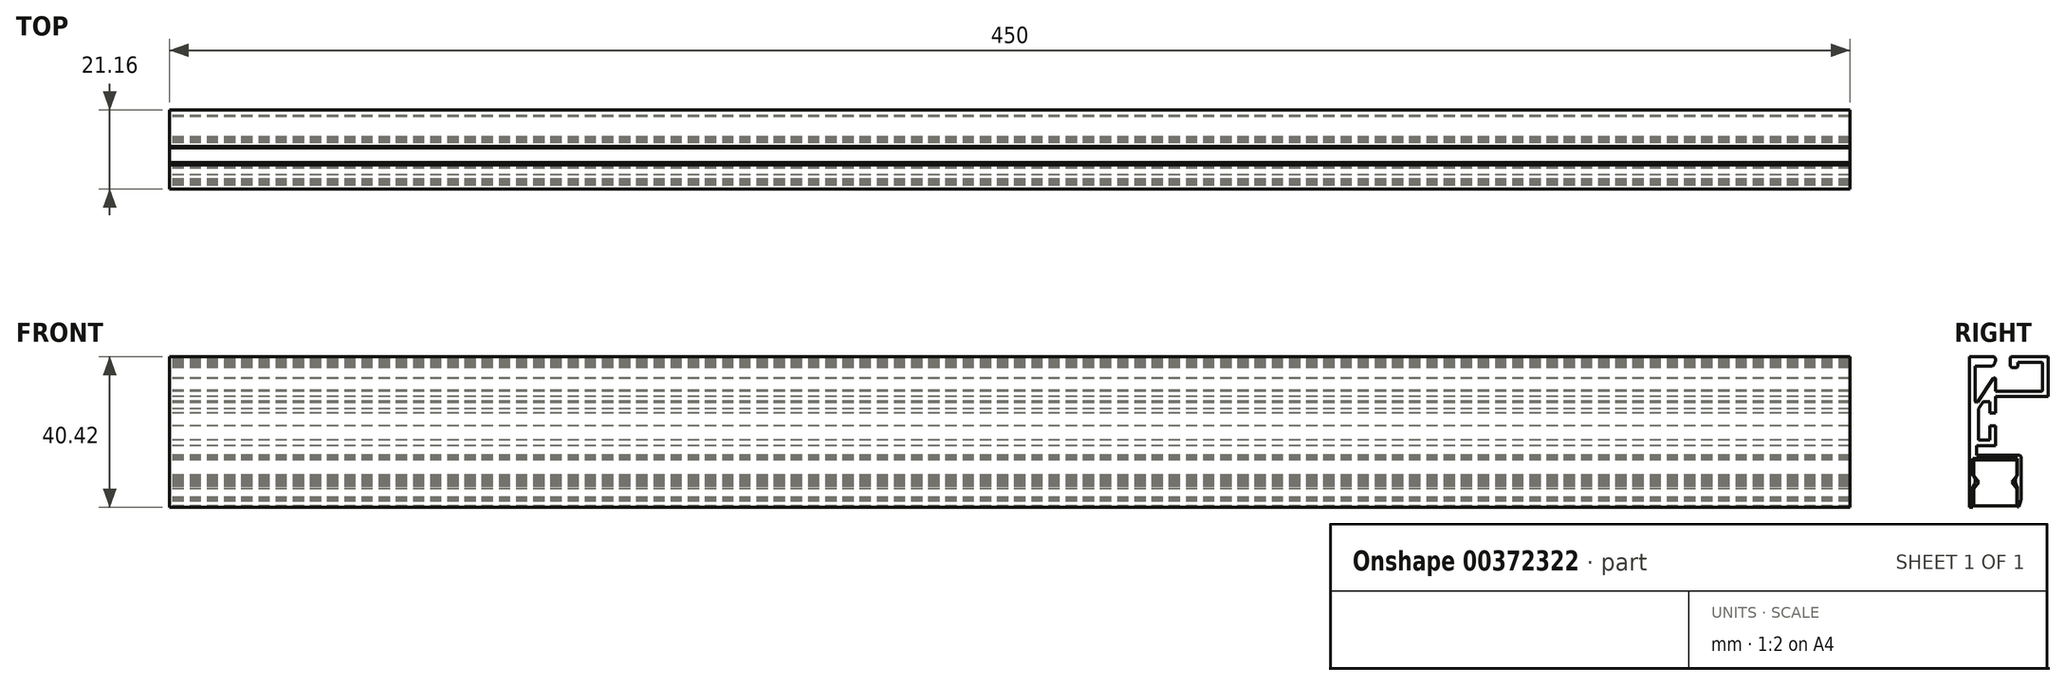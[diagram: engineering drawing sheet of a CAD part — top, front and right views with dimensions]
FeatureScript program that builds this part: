
annotation { "Feature Type Name" : "Feature", "Feature Type Description" : "" }
export const myFeature = defineFeature(function(context is Context, id is Id, definition is map)
    precondition{}
    {
        {
            var Q0;
            Q0=qCreatedBy(makeId("Right.planeOp"),FACE);
            var sketch = newSketch(context, id + "F0", { "sketchPlane" : qUnion([Q0])});
            skLineSegment(sketch, "E0.13", {"start": v(97.95, 20.2) * mm, "end": v(97.95, 9.58) * mm});
            skLineSegment(sketch, "E1.MirrorCS", {"start": v(83.74, 19.84) * mm, "end": v(83.78, 19.62) * mm});
            skLineSegment(sketch, "E2.MirrorCS", {"start": v(83.74, 18.76) * mm, "end": v(83.61, 18.51) * mm});
            skLineSegment(sketch, "E3.MirrorCS", {"start": v(83.78, 19.05) * mm, "end": v(83.74, 18.76) * mm});
            skLineSegment(sketch, "E4.MirrorCS", {"start": v(83.61, 18.51) * mm, "end": v(83.64, 18.5) * mm});
            skLineSegment(sketch, "E5.MirrorCS", {"start": v(83.2, 17.83) * mm, "end": v(83.2, 17.85) * mm});
            skLineSegment(sketch, "E6.MirrorCS", {"start": v(83.64, 18.5) * mm, "end": v(83.2, 17.83) * mm});
            skLineSegment(sketch, "E7.MirrorCS", {"start": v(83.8, 19.62) * mm, "end": v(83.8, 19.05) * mm});
            skLineSegment(sketch, "E8.MirrorCS", {"start": v(83.8, 19.05) * mm, "end": v(83.78, 19.05) * mm});
            skLineSegment(sketch, "E9.MirrorCS", {"start": v(77.92, -14.41) * mm, "end": v(77.8, -14.59) * mm});
            skLineSegment(sketch, "E10.MirrorCS", {"start": v(83.42, 20.16) * mm, "end": v(83.61, 20.04) * mm});
            skLineSegment(sketch, "E11.MirrorCS", {"start": v(82.78, 17.6) * mm, "end": v(82.78, 17.63) * mm});
            skLineSegment(sketch, "E12.MirrorCS", {"start": v(83.8, 19.62) * mm, "end": v(83.78, 19.62) * mm});
            skLineSegment(sketch, "E13.MirrorCS", {"start": v(78.16, -12.18) * mm, "end": v(78.3, -12.6) * mm});
            skLineSegment(sketch, "E14.MirrorCS", {"start": v(78.16, -14.02) * mm, "end": v(77.9, -14.41) * mm});
            skLineSegment(sketch, "E15.MirrorCS", {"start": v(83.2, 20.2) * mm, "end": v(83.42, 20.16) * mm});
            skLineSegment(sketch, "E16.MirrorCS", {"start": v(77.8, -11.61) * mm, "end": v(77.92, -11.79) * mm});
            skLineSegment(sketch, "E17.MirrorCS", {"start": v(83, 17.68) * mm, "end": v(82.78, 17.63) * mm});
            skLineSegment(sketch, "E18.MirrorCS", {"start": v(90.66, -18) * mm, "end": v(90.54, -18.5) * mm});
            skLineSegment(sketch, "E19.MirrorCS", {"start": v(78.3, -12.6) * mm, "end": v(78.36, -13.06) * mm});
            skLineSegment(sketch, "E20.MirrorCS", {"start": v(77.9, -11.79) * mm, "end": v(78.16, -12.18) * mm});
            skLineSegment(sketch, "E21.MirrorCS", {"start": v(83.2, 17.85) * mm, "end": v(83, 17.68) * mm});
            skLineSegment(sketch, "E22.MirrorCS", {"start": v(78.3, -13.6) * mm, "end": v(78.16, -14.02) * mm});
            skLineSegment(sketch, "E23.MirrorCS", {"start": v(83.61, 20.04) * mm, "end": v(83.74, 19.84) * mm});
            skLineSegment(sketch, "E24.MirrorCS", {"start": v(89.73, -14.59) * mm, "end": v(89.58, -14.41) * mm});
            skLineSegment(sketch, "E25.MirrorCS", {"start": v(90.56, -18.5) * mm, "end": v(90.54, -18.5) * mm});
            skLineSegment(sketch, "E26.MirrorCS", {"start": v(77.94, -11.74) * mm, "end": v(79.39, -13.5) * mm});
            skLineSegment(sketch, "E27.MirrorCS", {"start": v(78.36, -13.06) * mm, "end": v(78.36, -13.14) * mm});
            skLineSegment(sketch, "E28.MirrorCS", {"start": v(78.36, -13.14) * mm, "end": v(78.3, -13.6) * mm});
            skLineSegment(sketch, "E29.MirrorCS", {"start": v(77.9, -11.79) * mm, "end": v(77.92, -11.79) * mm});
            skLineSegment(sketch, "E30.MirrorCS", {"start": v(90.56, -18.5) * mm, "end": v(90.02, -20.01) * mm});
            skLineSegment(sketch, "E31.MirrorCS", {"start": v(89.58, -14.41) * mm, "end": v(89.6, -14.41) * mm});
            skLineSegment(sketch, "E32.MirrorCS", {"start": v(77.9, -14.41) * mm, "end": v(77.92, -14.41) * mm});
            skLineSegment(sketch, "E33.MirrorCS", {"start": v(89.33, -14.02) * mm, "end": v(89.19, -13.6) * mm});
            skLineSegment(sketch, "E34.MirrorCS", {"start": v(79.39, -13.5) * mm, "end": v(77.94, -15.25) * mm});
            skLineSegment(sketch, "E35.MirrorCS", {"start": v(89.58, -19.82) * mm, "end": v(89.58, -15.25) * mm});
            skLineSegment(sketch, "E36.MirrorCS", {"start": v(89.73, -20.01) * mm, "end": v(89.73, -14.59) * mm});
            skLineSegment(sketch, "E37.MirrorCS", {"start": v(89.14, -13.06) * mm, "end": v(89.14, -13.14) * mm});
            skLineSegment(sketch, "E38.MirrorCS", {"start": v(89.6, -14.41) * mm, "end": v(89.33, -14.02) * mm});
            skLineSegment(sketch, "E39.MirrorCS", {"start": v(90.02, -20.01) * mm, "end": v(89.73, -20.01) * mm});
            skLineSegment(sketch, "E40.MirrorCS", {"start": v(90.7, -6.88) * mm, "end": v(90.73, -6.88) * mm});
            skLineSegment(sketch, "E41.MirrorCS", {"start": v(89.19, -13.6) * mm, "end": v(89.14, -13.14) * mm});
            skLineSegment(sketch, "E42.MirrorCS", {"start": v(89.14, -13.06) * mm, "end": v(89.19, -12.6) * mm});
            skLineSegment(sketch, "E43.MirrorCS", {"start": v(90.68, -6.65) * mm, "end": v(90.7, -6.88) * mm});
            skLineSegment(sketch, "E44.MirrorCS", {"start": v(89.19, -12.6) * mm, "end": v(89.33, -12.18) * mm});
            skLineSegment(sketch, "E45.MirrorCS", {"start": v(89.6, -11.79) * mm, "end": v(89.58, -11.79) * mm});
            skLineSegment(sketch, "E46.MirrorCS", {"start": v(90.7, -17.5) * mm, "end": v(90.66, -18) * mm});
            skLineSegment(sketch, "E47.MirrorCS", {"start": v(89.33, -12.18) * mm, "end": v(89.6, -11.79) * mm});
            skLineSegment(sketch, "E48.MirrorCS", {"start": v(96.38, 11.05) * mm, "end": v(96.28, 10.95) * mm});
            skLineSegment(sketch, "E49.MirrorCS", {"start": v(90.41, -6.31) * mm, "end": v(90.59, -6.48) * mm});
            skLineSegment(sketch, "E50.MirrorCS", {"start": v(96.28, 10.95) * mm, "end": v(96.14, 10.9) * mm});
            skLineSegment(sketch, "E51.MirrorCS", {"start": v(89.58, -11.79) * mm, "end": v(89.73, -11.61) * mm});
            skLineSegment(sketch, "E52.MirrorCS", {"start": v(90.7, -17.5) * mm, "end": v(90.73, -17.5) * mm});
            skLineSegment(sketch, "E53.MirrorCS", {"start": v(96.43, 11.2) * mm, "end": v(96.46, 11.2) * mm});
            skLineSegment(sketch, "E54.MirrorCS", {"start": v(96.14, 10.9) * mm, "end": v(96.14, 10.88) * mm});
            skLineSegment(sketch, "E55.MirrorCS", {"start": v(96.43, 11.2) * mm, "end": v(96.38, 11.05) * mm});
            skLineSegment(sketch, "E56.MirrorCS", {"start": v(90.24, -6.21) * mm, "end": v(90.41, -6.31) * mm});
            skLineSegment(sketch, "E57.MirrorCS", {"start": v(89.58, -15.25) * mm, "end": v(88.1, -13.5) * mm});
            skLineSegment(sketch, "E58.MirrorCS", {"start": v(90.02, -6.19) * mm, "end": v(90.24, -6.21) * mm});
            skLineSegment(sketch, "E59.MirrorCS", {"start": v(90.73, -6.88) * mm, "end": v(90.73, -17.5) * mm});
            skLineSegment(sketch, "E60.MirrorCS", {"start": v(88.1, -13.5) * mm, "end": v(89.58, -11.74) * mm});
            skLineSegment(sketch, "E61.MirrorCS", {"start": v(90.02, -6.19) * mm, "end": v(90.02, -6.16) * mm});
            skLineSegment(sketch, "E62.MirrorCS", {"start": v(90.59, -6.48) * mm, "end": v(90.68, -6.65) * mm});
            skLineSegment(sketch, "E63.MirrorCS", {"start": v(89.58, -11.74) * mm, "end": v(89.58, -7.49) * mm});
            skLineSegment(sketch, "E64.MirrorCS", {"start": v(88.57, -18.8) * mm, "end": v(88.57, -15.62) * mm});
            skLineSegment(sketch, "E65.MirrorCS", {"start": v(80.7, -13.5) * mm, "end": v(78.95, -15.62) * mm});
            skLineSegment(sketch, "E66.MirrorCS", {"start": v(78.95, -11.37) * mm, "end": v(80.7, -13.5) * mm});
            skLineSegment(sketch, "E67.MirrorCS", {"start": v(87.52, -18.54) * mm, "end": v(88.57, -18.83) * mm});
            skLineSegment(sketch, "E68.MirrorCS", {"start": v(78.8, 7.96) * mm, "end": v(78.68, 7.93) * mm});
            skLineSegment(sketch, "E69.MirrorCS", {"start": v(78.53, 7.98) * mm, "end": v(78.43, 8.08) * mm});
            skLineSegment(sketch, "E70.MirrorCS", {"start": v(89.75, 17.5) * mm, "end": v(89.65, 17.36) * mm});
            skLineSegment(sketch, "E71.MirrorCS", {"start": v(89.73, -11.61) * mm, "end": v(89.73, -7.17) * mm});
            skLineSegment(sketch, "E72.MirrorCS", {"start": v(87.98, 17.36) * mm, "end": v(87.89, 17.5) * mm});
            skLineSegment(sketch, "E73.MirrorCS", {"start": v(87.81, 19.91) * mm, "end": v(87.86, 20.06) * mm});
            skLineSegment(sketch, "E74.MirrorCS", {"start": v(76.79, 20.2) * mm, "end": v(83.2, 20.2) * mm});
            skLineSegment(sketch, "E75.MirrorCS", {"start": v(87.86, 20.06) * mm, "end": v(87.96, 20.16) * mm});
            skLineSegment(sketch, "E76.MirrorCS", {"start": v(78.92, 8.05) * mm, "end": v(78.8, 7.96) * mm});
            skLineSegment(sketch, "E77.MirrorCS", {"start": v(87.81, 19.91) * mm, "end": v(87.81, 17.7) * mm});
            skLineSegment(sketch, "E78.MirrorCS", {"start": v(89.65, 17.36) * mm, "end": v(89.5, 17.26) * mm});
            skLineSegment(sketch, "E79.MirrorCS", {"start": v(83.32, 14.49) * mm, "end": v(83.61, 14.49) * mm});
            skLineSegment(sketch, "E80.MirrorCS", {"start": v(87.96, 20.16) * mm, "end": v(88.1, 20.2) * mm});
            skLineSegment(sketch, "E81.MirrorCS", {"start": v(87.89, 17.5) * mm, "end": v(87.84, 17.7) * mm});
            skLineSegment(sketch, "E82.MirrorCS", {"start": v(78.92, 8.05) * mm, "end": v(78.95, 8.05) * mm});
            skLineSegment(sketch, "E83.MirrorCS", {"start": v(88.13, 17.26) * mm, "end": v(87.98, 17.36) * mm});
            skLineSegment(sketch, "E84.MirrorCS", {"start": v(78.68, 7.93) * mm, "end": v(78.53, 7.98) * mm});
            skLineSegment(sketch, "E85.MirrorCS", {"start": v(88.33, 17.21) * mm, "end": v(89.3, 17.21) * mm});
            skLineSegment(sketch, "E86.MirrorCS", {"start": v(80.52, 8.08) * mm, "end": v(79.3, 6.24) * mm});
            skLineSegment(sketch, "E87.MirrorCS", {"start": v(77.8, -14.59) * mm, "end": v(77.8, -20.2) * mm});
            skLineSegment(sketch, "E88.MirrorCS", {"start": v(96.28, 18.66) * mm, "end": v(96.38, 18.56) * mm});
            skLineSegment(sketch, "E89.MirrorCS", {"start": v(82.78, 17.6) * mm, "end": v(78.38, 17.6) * mm});
            skLineSegment(sketch, "E90.MirrorCS", {"start": v(78.43, 8.08) * mm, "end": v(78.38, 8.23) * mm});
            skLineSegment(sketch, "E91.MirrorCS", {"start": v(88.57, -15.62) * mm, "end": v(86.8, -13.5) * mm});
            skLineSegment(sketch, "E92.MirrorCS", {"start": v(87.84, 17.7) * mm, "end": v(87.81, 17.7) * mm});
            skLineSegment(sketch, "E93.MirrorCS", {"start": v(86.8, -13.5) * mm, "end": v(88.57, -11.37) * mm});
            skLineSegment(sketch, "E94.MirrorCS", {"start": v(83.61, 14.49) * mm, "end": v(83.76, 14.44) * mm});
            skLineSegment(sketch, "E95.MirrorCS", {"start": v(88.33, 17.21) * mm, "end": v(88.13, 17.26) * mm});
            skLineSegment(sketch, "E96.MirrorCS", {"start": v(89.83, 17.7) * mm, "end": v(89.8, 17.7) * mm});
            skLineSegment(sketch, "E97.MirrorCS", {"start": v(89.5, 17.26) * mm, "end": v(89.3, 17.21) * mm});
            skLineSegment(sketch, "E98.MirrorCS", {"start": v(96.14, 18.71) * mm, "end": v(96.28, 18.66) * mm});
            skLineSegment(sketch, "E99.MirrorCS", {"start": v(78.95, -15.62) * mm, "end": v(78.95, -18.8) * mm});
            skLineSegment(sketch, "E100.MirrorCS", {"start": v(83.15, 14.39) * mm, "end": v(83.32, 14.49) * mm});
            skLineSegment(sketch, "E101.MirrorCS", {"start": v(77.94, -15.25) * mm, "end": v(77.94, -19.82) * mm});
            skLineSegment(sketch, "E102.MirrorCS", {"start": v(96.38, 18.56) * mm, "end": v(96.43, 18.42) * mm});
            skLineSegment(sketch, "E103.MirrorCS", {"start": v(77.8, -20.2) * mm, "end": v(76.79, -20.2) * mm});
            skLineSegment(sketch, "E104.MirrorCS", {"start": v(78.95, -18.83) * mm, "end": v(80, -18.54) * mm});
            skLineSegment(sketch, "E105.MirrorCS", {"start": v(88.57, -11.37) * mm, "end": v(88.57, -8.47) * mm});
            skLineSegment(sketch, "E106.MirrorCS", {"start": v(83.76, 14.44) * mm, "end": v(83.8, 14.3) * mm});
            skLineSegment(sketch, "E107.MirrorCS", {"start": v(89.83, 17.7) * mm, "end": v(89.83, 18.71) * mm});
            skLineSegment(sketch, "E108.MirrorCS", {"start": v(89.8, 17.7) * mm, "end": v(89.75, 17.5) * mm});
            skLineSegment(sketch, "E109.MirrorCS", {"start": v(77.94, -7.49) * mm, "end": v(77.94, -11.74) * mm});
            skLineSegment(sketch, "E110.MirrorCS", {"start": v(83.15, 14.39) * mm, "end": v(83.15, 14.41) * mm});
            skLineSegment(sketch, "E111.MirrorCS", {"start": v(96.43, 18.42) * mm, "end": v(96.46, 18.42) * mm});
            skLineSegment(sketch, "E112.MirrorCS", {"start": v(80, -18.54) * mm, "end": v(81.06, -18.34) * mm});
            skLineSegment(sketch, "E113.MirrorCS", {"start": v(77.8, -7.17) * mm, "end": v(77.8, -11.61) * mm});
            skLineSegment(sketch, "E114.MirrorCS", {"start": v(86.46, -18.34) * mm, "end": v(87.52, -18.54) * mm});
            skLineSegment(sketch, "E115.MirrorCS", {"start": v(80.52, 8.08) * mm, "end": v(81.4, 8.08) * mm});
            skLineSegment(sketch, "E116.MirrorCS", {"start": v(83.22, -18.12) * mm, "end": v(84.3, -18.12) * mm});
            skLineSegment(sketch, "E117.MirrorCS", {"start": v(84.3, -18.12) * mm, "end": v(85.38, -18.2) * mm});
            skLineSegment(sketch, "E118.MirrorCS", {"start": v(85.38, -18.2) * mm, "end": v(86.46, -18.34) * mm});
            skLineSegment(sketch, "E119.MirrorCS", {"start": v(78.95, -8.47) * mm, "end": v(78.95, -11.37) * mm});
            skLineSegment(sketch, "E120.MirrorCS", {"start": v(81.06, -18.34) * mm, "end": v(82.14, -18.2) * mm});
            skLineSegment(sketch, "E121.MirrorCS", {"start": v(82.14, -18.2) * mm, "end": v(83.22, -18.12) * mm});
            skLineSegment(sketch, "E122.MirrorCS", {"start": v(77.94, -19.82) * mm, "end": v(89.58, -19.82) * mm});
            skLineSegment(sketch, "E123.MirrorCS", {"start": v(82.29, 8.08) * mm, "end": v(81.4, 8.08) * mm});
            skLineSegment(sketch, "E124.MirrorCS", {"start": v(83.8, 14.3) * mm, "end": v(83.8, 10.88) * mm});
            skLineSegment(sketch, "E125.MirrorCS", {"start": v(82.29, 5.06) * mm, "end": v(82.29, 8.08) * mm});
            skLineSegment(sketch, "E126.MirrorCS", {"start": v(83.8, 5.06) * mm, "end": v(82.29, 5.06) * mm});
            skLineSegment(sketch, "E127.MirrorCS", {"start": v(89.83, 18.71) * mm, "end": v(96.14, 18.71) * mm});
            skLineSegment(sketch, "E128.MirrorCS", {"start": v(97.95, 20.2) * mm, "end": v(88.1, 20.2) * mm});
            skLineSegment(sketch, "E129.MirrorCS", {"start": v(83.8, 9.58) * mm, "end": v(83.8, 5.06) * mm});
            skLineSegment(sketch, "E130.MirrorCS", {"start": v(78.78, -3.66) * mm, "end": v(78.78, -6.16) * mm});
            skLineSegment(sketch, "E131.MirrorCS", {"start": v(82.29, -2.16) * mm, "end": v(82.29, 1.65) * mm});
            skLineSegment(sketch, "E132.MirrorCS", {"start": v(82.29, -2.16) * mm, "end": v(79.3, -2.16) * mm});
            skLineSegment(sketch, "E133.MirrorCS", {"start": v(83.8, -3.66) * mm, "end": v(78.78, -3.66) * mm});
            skLineSegment(sketch, "E134.MirrorCS", {"start": v(78.95, 8.05) * mm, "end": v(83.15, 14.41) * mm});
            skLineSegment(sketch, "E135.MirrorCS", {"start": v(82.29, 1.65) * mm, "end": v(83.8, 1.65) * mm});
            skLineSegment(sketch, "E136.MirrorCS", {"start": v(90.02, -6.16) * mm, "end": v(78.78, -6.16) * mm});
            skLineSegment(sketch, "E137.MirrorCS", {"start": v(83.8, 1.65) * mm, "end": v(83.8, -3.66) * mm});
            skLineSegment(sketch, "E138.MirrorCS", {"start": v(76.79, 20.2) * mm, "end": v(76.79, -20.2) * mm});
            skLineSegment(sketch, "E139.MirrorCS", {"start": v(77.8, -7.17) * mm, "end": v(89.73, -7.17) * mm});
            skPoint(sketch, "E140.MirrorP", {"position": v(89.11, -13.14) * mm});
            skLineSegment(sketch, "E141.MirrorCS", {"start": v(79.3, 6.24) * mm, "end": v(79.3, -2.16) * mm});
            skLineSegment(sketch, "E142.MirrorCS", {"start": v(83.8, 10.88) * mm, "end": v(96.14, 10.88) * mm});
            skLineSegment(sketch, "E143.MirrorCS", {"start": v(89.58, -7.49) * mm, "end": v(77.94, -7.49) * mm});
            skLineSegment(sketch, "E144.MirrorCS", {"start": v(88.57, -8.47) * mm, "end": v(78.95, -8.47) * mm});
            skPoint(sketch, "E145.MirrorP", {"position": v(82.29, 8.08) * mm});
            skLineSegment(sketch, "E146.MirrorCS", {"start": v(83.8, 9.58) * mm, "end": v(97.95, 9.58) * mm});
            skLineSegment(sketch, "E147.MirrorCS", {"start": v(78.38, 17.6) * mm, "end": v(78.38, 8.23) * mm});
            skPoint(sketch, "E148.MirrorP", {"position": v(89.11, -13.06) * mm});
            skPoint(sketch, "E149.MirrorP", {"position": v(83.05, 5.06) * mm});
            skLineSegment(sketch, "E150.MirrorCS", {"start": v(96.46, 18.42) * mm, "end": v(96.46, 11.2) * mm});
            skPoint(sketch, "E151.MirrorP", {"position": v(81.4, 8.08) * mm});
            skSolve(sketch);
        }
        {
            var Q0;
            Q0=qSketchRegion(id+"F0",true);
            extrude(context, id + "F1", {"entities" : qUnion([Q0]), "offsetDistance" : 25 * mm, "depth" : 450 * mm});
        }
    });
